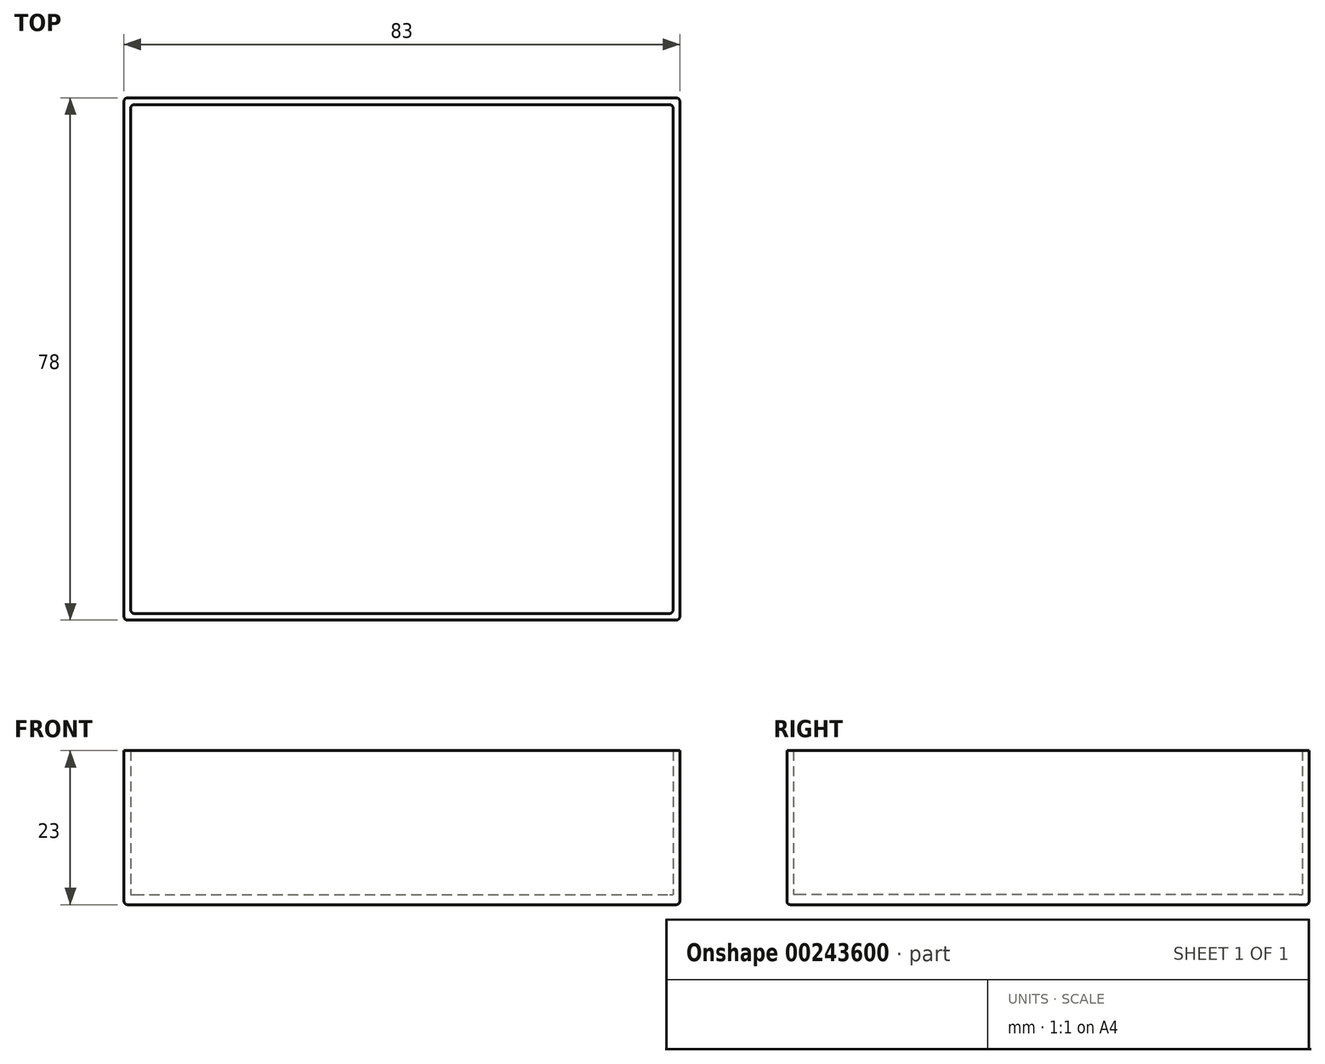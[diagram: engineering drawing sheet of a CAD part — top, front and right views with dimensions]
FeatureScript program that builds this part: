
annotation { "Feature Type Name" : "Feature", "Feature Type Description" : "" }
export const myFeature = defineFeature(function(context is Context, id is Id, definition is map)
    precondition{}
    {
        {
            var Q0;
            Q0=qCreatedBy(makeId("Top.planeOp"),FACE);
            var sketch = newSketch(context, id + "F0", { "sketchPlane" : qUnion([Q0])});
            skLineSegment(sketch, "E0.bottom", {"start": v(-41.5, 39) * mm, "end": v(41.5, 39) * mm});
            skLineSegment(sketch, "E0.top", {"start": v(-41.5, -39) * mm, "end": v(41.5, -39) * mm});
            skLineSegment(sketch, "E0.left", {"start": v(-41.5, 39) * mm, "end": v(-41.5, -39) * mm});
            skLineSegment(sketch, "E0.right", {"start": v(41.5, 39) * mm, "end": v(41.5, -39) * mm});
            skLineSegment(sketch, "E1.bottom", {"start": v(-40.5, 38) * mm, "end": v(40.5, 38) * mm});
            skLineSegment(sketch, "E1.top", {"start": v(-40.5, -38) * mm, "end": v(40.5, -38) * mm});
            skLineSegment(sketch, "E1.left", {"start": v(-40.5, 38) * mm, "end": v(-40.5, -38) * mm});
            skLineSegment(sketch, "E1.right", {"start": v(40.5, 38) * mm, "end": v(40.5, -38) * mm});
            skSolve(sketch);
        }
        {
            var Q0;
            Q0=makeQuery(id+"F0.imprint","IMPRINT",FACE,{"disambiguationData":[TD([[makeQuery(id+"F0.imprint","IMPRINT",EDGE,{"derivedFrom":sQuery(id+"F0.wireOp",EDGE,"E0.bottom")}),-1.0]])]});
            extrude(context, id + "F1", {"entities" : qUnion([Q0]), "depth" : 23 * mm});
        }
        {
            var Q0;
            Q0=makeQuery(id+"F0.imprint","IMPRINT",FACE,{"disambiguationData":[TD([[makeQuery(id+"F0.imprint","IMPRINT",EDGE,{"derivedFrom":sQuery(id+"F0.wireOp",EDGE,"E1.bottom")}),-1.0]])]});
            extrude(context, id + "F2", {"entities" : qUnion([Q0]), "operationType" : NewBodyOperationType.ADD, "depth" : 1.5 * mm});
        }
        {
            var Q0;
            Q0=makeQuery(id+"F1.opExtrude","CAP_EDGE",EDGE,{"disambiguationData":[OSD([sQuery(id+"F0.wireOp",EDGE,"E0.top")])],"isStart":true});
            var Q1;
            Q1=makeQuery(id+"F1.opExtrude","CAP_EDGE",EDGE,{"disambiguationData":[OSD([sQuery(id+"F0.wireOp",EDGE,"E0.left")])],"isStart":true});
            var Q2;
            Q2=makeQuery(id+"F1.opExtrude","CAP_EDGE",EDGE,{"disambiguationData":[OSD([sQuery(id+"F0.wireOp",EDGE,"E0.bottom")])],"isStart":true});
            var Q3;
            Q3=makeQuery(id+"F1.opExtrude","CAP_EDGE",EDGE,{"disambiguationData":[OSD([sQuery(id+"F0.wireOp",EDGE,"E0.right")])],"isStart":true});
            var Q4;
            Q4=makeQuery(id+"F1.opExtrude","SWEPT_EDGE",EDGE,{"disambiguationData":[OSD([sQuery(id+"F0.wireOp",EDGE,"E0.top"),sQuery(id+"F0.wireOp",EDGE,"E0.left")])]});
            var Q5;
            Q5=makeQuery(id+"F1.opExtrude","SWEPT_EDGE",EDGE,{"disambiguationData":[OSD([sQuery(id+"F0.wireOp",EDGE,"E0.top"),sQuery(id+"F0.wireOp",EDGE,"E0.right")])]});
            var Q6;
            Q6=makeQuery(id+"F1.opExtrude","SWEPT_EDGE",EDGE,{"disambiguationData":[OSD([sQuery(id+"F0.wireOp",EDGE,"E0.bottom"),sQuery(id+"F0.wireOp",EDGE,"E0.left")])]});
            var Q7;
            Q7=makeQuery(id+"F1.opExtrude","SWEPT_EDGE",EDGE,{"disambiguationData":[OSD([sQuery(id+"F0.wireOp",EDGE,"E0.bottom"),sQuery(id+"F0.wireOp",EDGE,"E0.right")])]});
            fillet(context, id + "F3", {"entities" : qUnion([Q0, Q1, Q2, Q3, Q4, Q5, Q6, Q7]), "radius" : 0.5 * mm, "tangentPropagation" : true, "allowEdgeOverflow" : false});
        }
        {
            var Q0;
            Q0=makeQuery(id+"F1.opExtrude","SWEPT_EDGE",EDGE,{"disambiguationData":[OSD([sQuery(id+"F0.wireOp",EDGE,"E1.bottom"),sQuery(id+"F0.wireOp",EDGE,"E1.right")])]});
            var Q1;
            Q1=makeQuery(id+"F2.opExtrude","CAP_EDGE",EDGE,{"disambiguationData":[OSD([sQuery(id+"F0.wireOp",EDGE,"E1.bottom")])],"isStart":false});
            var Q2;
            Q2=makeQuery(id+"F2.opExtrude","CAP_EDGE",EDGE,{"disambiguationData":[OSD([sQuery(id+"F0.wireOp",EDGE,"E1.right")])],"isStart":false});
            var Q3;
            Q3=makeQuery(id+"F1.opExtrude","SWEPT_EDGE",EDGE,{"disambiguationData":[OSD([sQuery(id+"F0.wireOp",EDGE,"E1.bottom"),sQuery(id+"F0.wireOp",EDGE,"E1.left")])]});
            var Q4;
            Q4=makeQuery(id+"F2.opExtrude","CAP_EDGE",EDGE,{"disambiguationData":[OSD([sQuery(id+"F0.wireOp",EDGE,"E1.left")])],"isStart":false});
            var Q5;
            Q5=makeQuery(id+"F1.opExtrude","SWEPT_EDGE",EDGE,{"disambiguationData":[OSD([sQuery(id+"F0.wireOp",EDGE,"E1.top"),sQuery(id+"F0.wireOp",EDGE,"E1.right")])]});
            var Q6;
            Q6=makeQuery(id+"F2.opExtrude","CAP_EDGE",EDGE,{"disambiguationData":[OSD([sQuery(id+"F0.wireOp",EDGE,"E1.top")])],"isStart":false});
            var Q7;
            Q7=makeQuery(id+"F1.opExtrude","SWEPT_EDGE",EDGE,{"disambiguationData":[OSD([sQuery(id+"F0.wireOp",EDGE,"E1.top"),sQuery(id+"F0.wireOp",EDGE,"E1.left")])]});
            fillet(context, id + "F4", {"entities" : qUnion([Q0, Q1, Q2, Q3, Q4, Q5, Q6, Q7]), "radius" : 0.5 * mm, "tangentPropagation" : true, "allowEdgeOverflow" : false});
        }
    });
